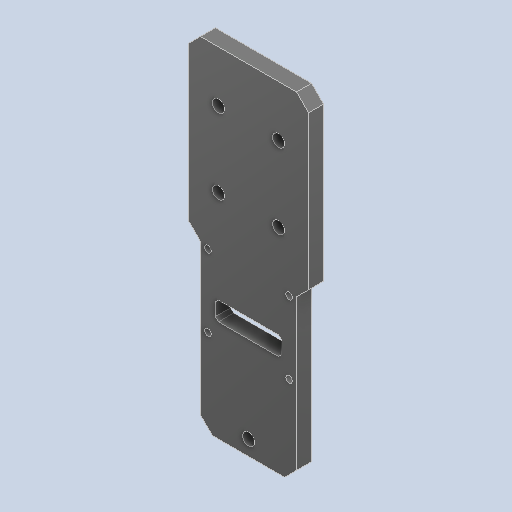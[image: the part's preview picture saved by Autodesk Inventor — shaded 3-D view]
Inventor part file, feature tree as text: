
AUTODESK INVENTOR PART (.ipt)
format: ipt  version: 2024.2 (Build 282272000, 272)  size: 255,488 bytes
history: native  units: in
note: dims shown in document units (in); Inventor stores cm internally (conversion verified against a paired STEP export)
features: extrude x1, chamfer x1, sketch x1, other x1
ambient origin geometry x8: Origin, YZ Plane, XZ Plane, XY Plane, X Axis, Y Axis, Z Axis, Center Point
bodies: Solid1 (feature_tree)
feature tree (4):
  extrude  "Extrusion1"  Depth=0.0787in
  chamfer  "Chamfer1"  Distance=0.2441in
  sketch  "Sketch1"  dims[d0=1.3307in d1=0.4331in d2=0.2441in d3=0.8661in d4=0.3937in d5=0.0in d6=0.0394in d7=0.0787in d8=45.0deg]
  other  "Cortar-Extruir9"
